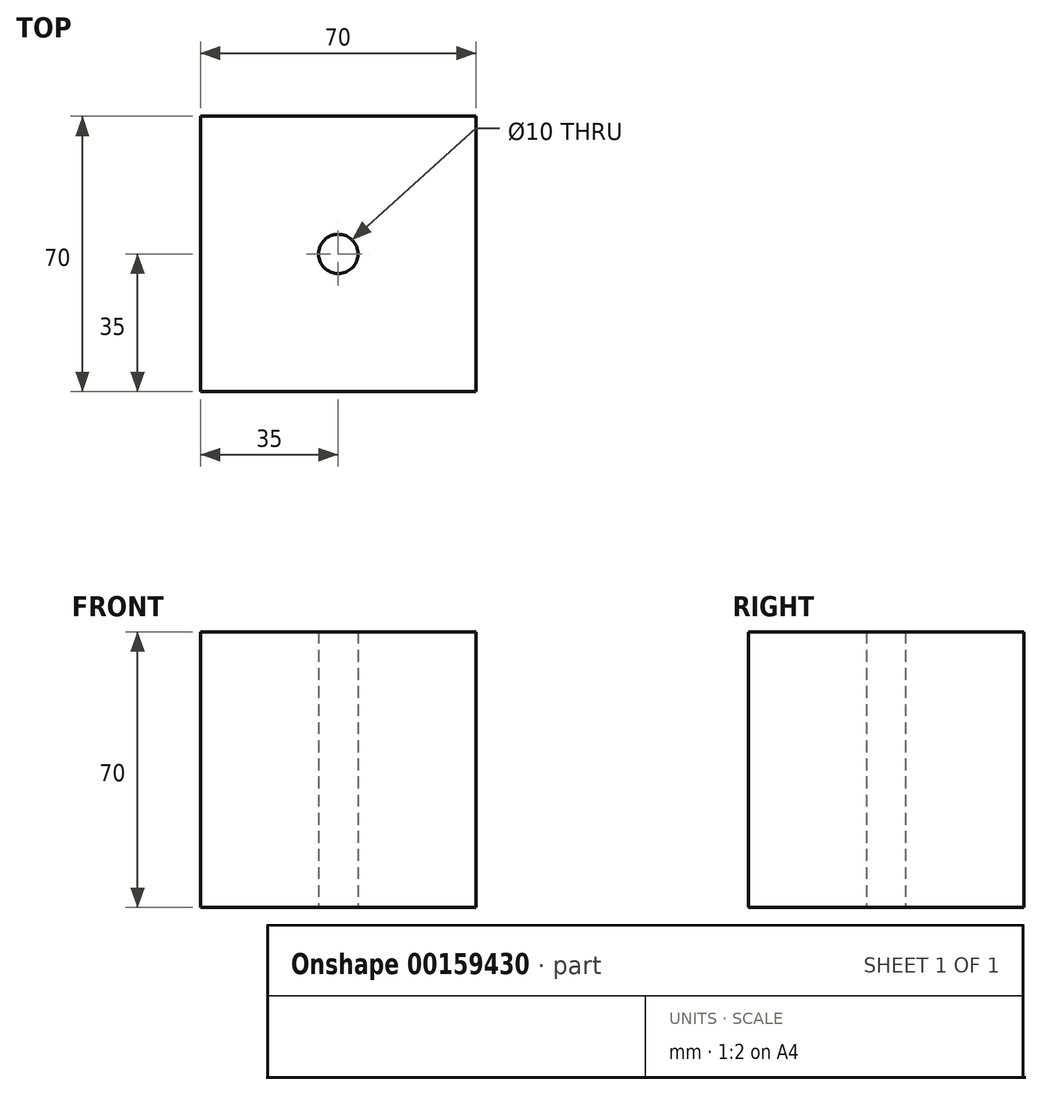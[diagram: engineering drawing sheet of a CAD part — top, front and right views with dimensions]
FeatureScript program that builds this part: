
annotation { "Feature Type Name" : "Feature", "Feature Type Description" : "" }
export const myFeature = defineFeature(function(context is Context, id is Id, definition is map)
    precondition{}
    {
        {
            var Q0;
            Q0=qCreatedBy(makeId("Top.planeOp"),FACE);
            var sketch = newSketch(context, id + "F0", { "sketchPlane" : qUnion([Q0])});
            skLineSegment(sketch, "E0.bottom", {"start": v(35, 35) * mm, "end": v(-35, 35) * mm});
            skLineSegment(sketch, "E0.top", {"start": v(35, -35) * mm, "end": v(-35, -35) * mm});
            skLineSegment(sketch, "E0.left", {"start": v(35, 35) * mm, "end": v(35, -35) * mm});
            skLineSegment(sketch, "E0.right", {"start": v(-35, 35) * mm, "end": v(-35, -35) * mm});
            skPoint(sketch, "E0.middle", {"position": v(0, 0) * mm});
            skCircle(sketch, "E1", {"center": v(0, 0) * mm, "radius": 5 * mm});
            skSolve(sketch);
        }
        {
            var Q0;
            Q0 = qSketchRegion(id + "F0", true);
            extrude(context, id + "F1", {"entities" : qUnion([Q0]), "depth" : 70 * mm});
        }
    });
